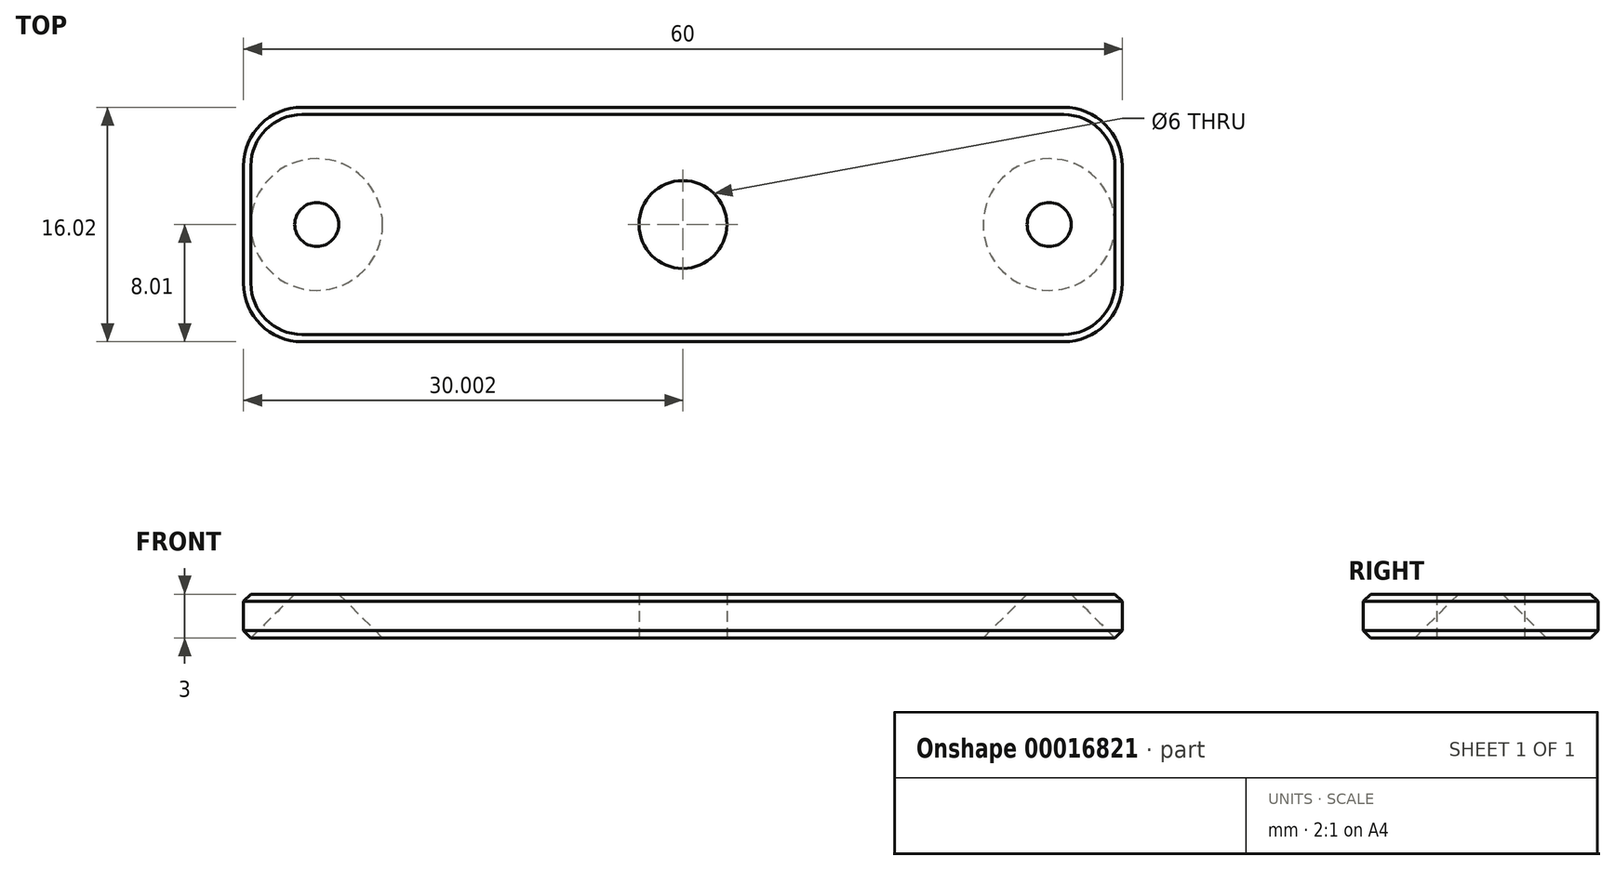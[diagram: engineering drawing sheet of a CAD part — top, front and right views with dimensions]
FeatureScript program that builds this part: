
annotation { "Feature Type Name" : "Feature", "Feature Type Description" : "" }
export const myFeature = defineFeature(function(context is Context, id is Id, definition is map)
    precondition{}
    {
        {
            var Q0;
            Q0=qCreatedBy(makeId("Top.planeOp"),FACE);
            var sketch = newSketch(context, id + "F0", { "sketchPlane" : qUnion([Q0])});
            skLineSegment(sketch, "E0.bottom", {"start": v(-25.99, 8.35) * mm, "end": v(26.01, 8.35) * mm});
            skLineSegment(sketch, "E0.top", {"start": v(-25.99, -7.67) * mm, "end": v(26.01, -7.67) * mm});
            skLineSegment(sketch, "E0.left", {"start": v(-29.99, 4.35) * mm, "end": v(-29.99, -3.67) * mm});
            skLineSegment(sketch, "E0.right", {"start": v(30.01, 4.35) * mm, "end": v(30.01, -3.67) * mm});
            skLineSegment(sketch, "E1", {"start": v(-29.99, 8.35) * mm, "end": v(30.01, -7.67) * mm, "construction": true});
            skLineSegment(sketch, "E2", {"start": v(30.01, 8.35) * mm, "end": v(-29.99, -7.67) * mm, "construction": true});
            skLineSegment(sketch, "E3", {"start": v(-29.99, 0.34) * mm, "end": v(30.01, 0.34) * mm, "construction": true});
            skCircle(sketch, "E4", {"center": v(0.01, 0.34) * mm, "radius": 3 * mm});
            skCircle(sketch, "E5", {"center": v(0.01, 0.34) * mm, "radius": 25 * mm, "construction": true});
            skCircle(sketch, "E6", {"center": v(-24.99, 0.34) * mm, "radius": 1.5 * mm});
            skCircle(sketch, "E7", {"center": v(25.01, 0.34) * mm, "radius": 1.5 * mm});
            skPoint(sketch, "E8.visualSharp", {"position": v(30.01, -7.67) * mm});
            skArc(sketch, "E8.filletArc", {"start": v(26.01, -7.67) * mm, "mid": v(28.84, -6.5) * mm, "end": v(30.01, -3.67) * mm});
            skPoint(sketch, "E9.visualSharp", {"position": v(-29.99, -7.67) * mm});
            skArc(sketch, "E9.filletArc", {"start": v(-29.99, -3.67) * mm, "mid": v(-28.82, -6.5) * mm, "end": v(-25.99, -7.67) * mm});
            skPoint(sketch, "E10.visualSharp", {"position": v(-29.99, 8.35) * mm});
            skArc(sketch, "E10.filletArc", {"start": v(-25.99, 8.35) * mm, "mid": v(-28.82, 7.18) * mm, "end": v(-29.99, 4.35) * mm});
            skPoint(sketch, "E11.visualSharp", {"position": v(30.01, 8.35) * mm});
            skArc(sketch, "E11.filletArc", {"start": v(30.01, 4.35) * mm, "mid": v(28.84, 7.18) * mm, "end": v(26.01, 8.35) * mm});
            skSolve(sketch);
        }
        {
            var Q0;
            Q0 = qSketchRegion(id + "F0", true);
            extrude(context, id + "F1", {"entities" : qUnion([Q0]), "depth" : 3 * mm});
        }
        {
            var Q0;
            Q0=makeQuery(id+"F1.opExtrude","CAP_EDGE",EDGE,{"disambiguationData":[OSD([sQuery(id+"F0.wireOp",EDGE,"E6")])],"isStart":true});
            var Q1;
            Q1=makeQuery(id+"F1.opExtrude","CAP_EDGE",EDGE,{"disambiguationData":[OSD([sQuery(id+"F0.wireOp",EDGE,"E7")])],"isStart":true});
            chamfer(context, id + "F2", {"entities" : qUnion([Q0, Q1]), "width" : 3 * mm, "tangentPropagation" : true});
        }
        {
            var Q0;
            Q0=makeQuery(id+"F1.opExtrude","CAP_EDGE",EDGE,{"disambiguationData":[OSD([sQuery(id+"F0.wireOp",EDGE,"E0.left")])],"isStart":false});
            var Q1;
            Q1=makeQuery(id+"F1.opExtrude","CAP_EDGE",EDGE,{"disambiguationData":[OSD([sQuery(id+"F0.wireOp",EDGE,"E9.filletArc")])],"isStart":false});
            var Q2;
            Q2=makeQuery(id+"F1.opExtrude","CAP_EDGE",EDGE,{"disambiguationData":[OSD([sQuery(id+"F0.wireOp",EDGE,"E0.top")])],"isStart":false});
            var Q3;
            Q3=makeQuery(id+"F1.opExtrude","CAP_EDGE",EDGE,{"disambiguationData":[OSD([sQuery(id+"F0.wireOp",EDGE,"E8.filletArc")])],"isStart":false});
            var Q4;
            Q4=makeQuery(id+"F1.opExtrude","CAP_EDGE",EDGE,{"disambiguationData":[OSD([sQuery(id+"F0.wireOp",EDGE,"E0.right")])],"isStart":false});
            var Q5;
            Q5=makeQuery(id+"F1.opExtrude","CAP_EDGE",EDGE,{"disambiguationData":[OSD([sQuery(id+"F0.wireOp",EDGE,"E11.filletArc")])],"isStart":false});
            var Q6;
            Q6=makeQuery(id+"F1.opExtrude","CAP_EDGE",EDGE,{"disambiguationData":[OSD([sQuery(id+"F0.wireOp",EDGE,"E0.bottom")])],"isStart":false});
            var Q7;
            Q7=makeQuery(id+"F1.opExtrude","CAP_EDGE",EDGE,{"disambiguationData":[OSD([sQuery(id+"F0.wireOp",EDGE,"E10.filletArc")])],"isStart":false});
            chamfer(context, id + "F3", {"entities" : qUnion([Q0, Q1, Q2, Q3, Q4, Q5, Q6, Q7]), "width" : 0.5 * mm, "tangentPropagation" : true});
        }
        {
            var Q0;
            Q0=makeQuery(id+"F1.opExtrude","CAP_EDGE",EDGE,{"disambiguationData":[OSD([sQuery(id+"F0.wireOp",EDGE,"E0.top")])],"isStart":true});
            var Q1;
            Q1=makeQuery(id+"F1.opExtrude","CAP_EDGE",EDGE,{"disambiguationData":[OSD([sQuery(id+"F0.wireOp",EDGE,"E9.filletArc")])],"isStart":true});
            var Q2;
            Q2=makeQuery(id+"F1.opExtrude","CAP_EDGE",EDGE,{"disambiguationData":[OSD([sQuery(id+"F0.wireOp",EDGE,"E0.left")])],"isStart":true});
            var Q3;
            Q3=makeQuery(id+"F1.opExtrude","CAP_EDGE",EDGE,{"disambiguationData":[OSD([sQuery(id+"F0.wireOp",EDGE,"E10.filletArc")])],"isStart":true});
            var Q4;
            Q4=makeQuery(id+"F1.opExtrude","CAP_EDGE",EDGE,{"disambiguationData":[OSD([sQuery(id+"F0.wireOp",EDGE,"E0.bottom")])],"isStart":true});
            var Q5;
            Q5=makeQuery(id+"F1.opExtrude","CAP_EDGE",EDGE,{"disambiguationData":[OSD([sQuery(id+"F0.wireOp",EDGE,"E11.filletArc")])],"isStart":true});
            var Q6;
            Q6=makeQuery(id+"F1.opExtrude","CAP_EDGE",EDGE,{"disambiguationData":[OSD([sQuery(id+"F0.wireOp",EDGE,"E0.right")])],"isStart":true});
            var Q7;
            Q7=makeQuery(id+"F1.opExtrude","CAP_EDGE",EDGE,{"disambiguationData":[OSD([sQuery(id+"F0.wireOp",EDGE,"E8.filletArc")])],"isStart":true});
            chamfer(context, id + "F4", {"entities" : qUnion([Q0, Q1, Q2, Q3, Q4, Q5, Q6, Q7]), "width" : 0.5 * mm, "tangentPropagation" : true});
        }
    });
